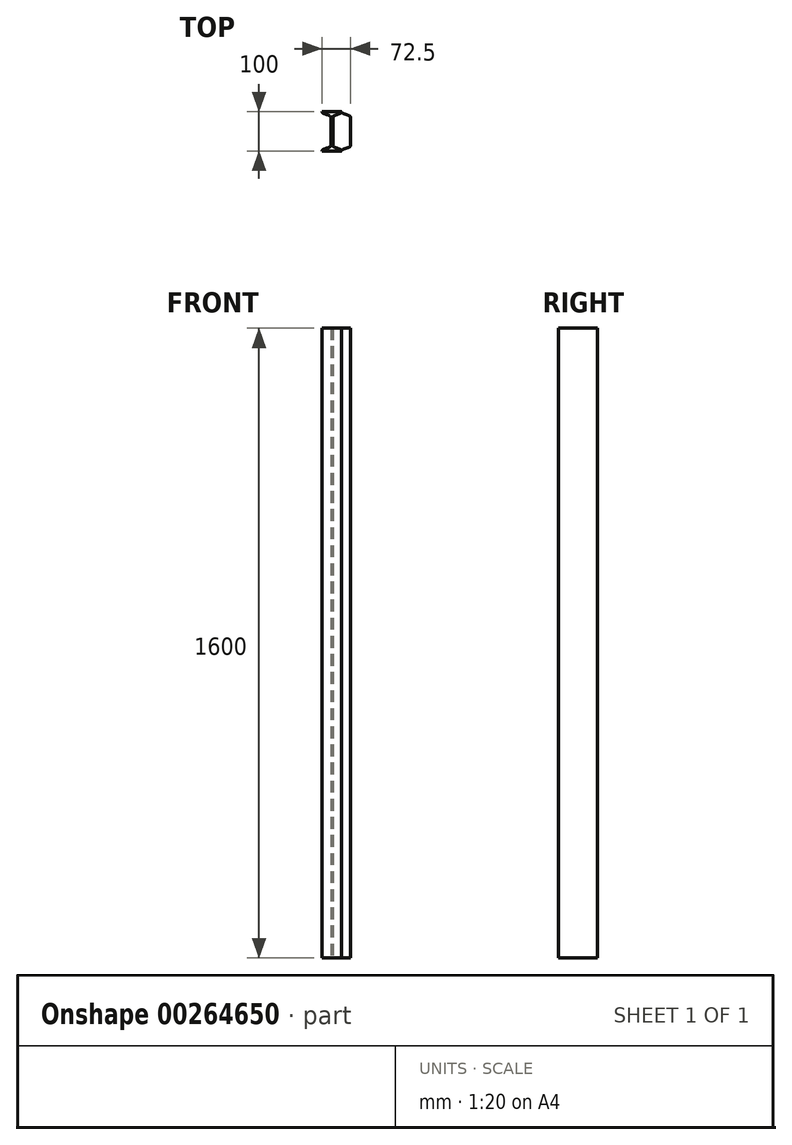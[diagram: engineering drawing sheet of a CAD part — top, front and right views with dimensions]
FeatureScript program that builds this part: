
annotation { "Feature Type Name" : "Feature", "Feature Type Description" : "" }
export const myFeature = defineFeature(function(context is Context, id is Id, definition is map)
    precondition{}
    {
        {
            var Q0;
            Q0=qCreatedBy(makeId("Top.planeOp"),FACE);
            var sketch = newSketch(context, id + "F0", { "sketchPlane" : qUnion([Q0])});
            skLineSegment(sketch, "E0", {"start": v(0, 0) * mm, "end": v(50, 0) * mm});
            skLineSegment(sketch, "E1", {"start": v(27.5, 14.62) * mm, "end": v(27.5, 85.38) * mm});
            skLineSegment(sketch, "E2", {"start": v(27.5, 85.38) * mm, "end": v(22.5, 85.38) * mm, "construction": true});
            skLineSegment(sketch, "E3", {"start": v(22.5, 85.38) * mm, "end": v(22.5, 14.62) * mm});
            skLineSegment(sketch, "E4", {"start": v(22.5, 14.62) * mm, "end": v(27.5, 14.62) * mm, "construction": true});
            skLineSegment(sketch, "E5", {"start": v(0, 100) * mm, "end": v(50, 100) * mm});
            skFitSpline(sketch, "E6", {"points": [v(50, 0) * mm, v(27.5, 14.62) * mm], "startDerivative": vector(0, 21) * mm, "endDerivative": vector(0, 22.88) * mm});
            skLineSegment(sketch, "E7", {"start": v(25, 14.62) * mm, "end": v(25, 0) * mm, "construction": true});
            skLineSegment(sketch, "E8", {"start": v(25, 100) * mm, "end": v(25, 85.38) * mm, "construction": true});
            skLineSegment(sketch, "E9", {"start": v(22.5, 50) * mm, "end": v(27.5, 50) * mm, "construction": true});
            skFitSpline(sketch, "E10.MirrorCS", {"points": [v(0, 0) * mm, v(22.5, 14.62) * mm], "startDerivative": vector(0, 21) * mm, "endDerivative": vector(0, 22.88) * mm});
            skFitSpline(sketch, "E11.MirrorCS", {"points": [v(0, 100) * mm, v(22.5, 85.38) * mm], "startDerivative": vector(0, -21) * mm, "endDerivative": vector(0, -22.87) * mm});
            skFitSpline(sketch, "E12.MirrorCS", {"points": [v(50, 100) * mm, v(27.5, 85.38) * mm], "startDerivative": vector(0, -21) * mm, "endDerivative": vector(0, -22.88) * mm});
            skLineSegment(sketch, "E13", {"start": v(50, 100) * mm, "end": v(50, 0) * mm, "construction": true});
            skLineSegment(sketch, "E14.MirrorCS", {"start": v(72.5, 14.62) * mm, "end": v(72.5, 85.38) * mm});
            skFitSpline(sketch, "E15.MirrorCS", {"points": [v(50, 0) * mm, v(72.5, 14.62) * mm], "startDerivative": vector(0, 21) * mm, "endDerivative": vector(0, 22.88) * mm});
            skFitSpline(sketch, "E16.MirrorCS", {"points": [v(50, 100) * mm, v(72.5, 85.38) * mm], "startDerivative": vector(0, -21) * mm, "endDerivative": vector(0, -22.88) * mm});
            skSolve(sketch);
        }
        {
            var Q0;
            {var subQ1=sQuery(id+"F0.wireOp",EDGE,"E0");Q0=makeQuery(id+"F0.imprint","IMPRINT",FACE,{"disambiguationData":[TD([[makeQuery(id+"F0.imprint","IMPRINT",EDGE,{"derivedFrom":subQ1}),1.0]])]});}
            extrude(context, id + "F1", {"entities" : qUnion([Q0]), "depth" : 1600 * mm, "offsetDistance" : 25 * mm});
        }
        {
            var Q0;
            Q0=makeQuery(id+"F0.imprint","IMPRINT",FACE,{"disambiguationData":[TD([[makeQuery(id+"F0.imprint","IMPRINT",EDGE,{"derivedFrom":sQuery(id+"F0.wireOp",EDGE,"E1")}),-1.0]])]});
            extrude(context, id + "F2", {"entities" : qUnion([Q0]), "depth" : 1600 * mm});
        }
    });
